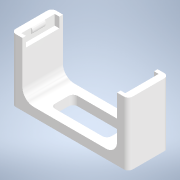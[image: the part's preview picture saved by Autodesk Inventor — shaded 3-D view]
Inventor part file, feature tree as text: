
AUTODESK INVENTOR PART (.ipt)
format: ipt  version: 2021 (Build 250183000, 183)  size: 235,520 bytes
history: mixed  units: in
note: dims shown in document units (in); Inventor stores cm internally (conversion verified against a paired STEP export)
features: extrude x6, sketch x6, projected_geometry x6, fillet x2, mirror x1, imported_body x1
ambient origin geometry x8: Origin, YZ Plane, XZ Plane, XY Plane, X Axis, Y Axis, Z Axis, Center Point
bodies: Solid1 (imported_parasolid)
feature tree (22):
  extrude  "Extrusion1"  Depth=0.0984in
  extrude  "Extrusion5"  Depth=0.2362in
  extrude  "Extrusion2"  Depth=0.3937in TaperAngle=0.0deg
  mirror  "Mirror1"
  extrude  "Extrusion3"  Depth=0.1969in
  extrude  "Extrusion4"  Depth=0.3937in
  fillet  "Fillet4"  Radius=0.3937in
  extrude  "Extrusion6"  Depth=0.2362in
  sketch  "Sketch1"  dims[d0=0.0984in d1=0.0in d3=0.0984in]
  projected_geometry  "Projected Loop1"
  projected_geometry  "Projected Loop2"
  sketch  "Sketch2"  dims[d4=0.2362in d5=0.0in d7=0.0394in]
  projected_geometry  "Projected Loop3"
  sketch  "Sketch3"  dims[d8=0.0394in d9=0.3937in d10=0.7874in d11=0.0in d12=0.0in]
  sketch  "Sketch4"  dims[d14=0.0394in d15=0.0in d16=0.1969in]
  projected_geometry  "Projected Loop4"
  sketch  "Sketch6"  dims[d17=0.5827in d18=0.5551in d19=0.3937in d20=0.0in]
  sketch  "Sketch7"  dims[d22=0.0197in d23=0.0in d24=0.0197in d25=0.2362in]
  projected_geometry  "Projected Loop5"
  projected_geometry  "Projected Loop6"
  fillet  "Fillet2"  Radius=0.2362in
  imported_body  NMx_Import_Brep_tag  [imported B-rep: ~38 faces, bbox_mm=[52.0, 28.0, 18.0]]
